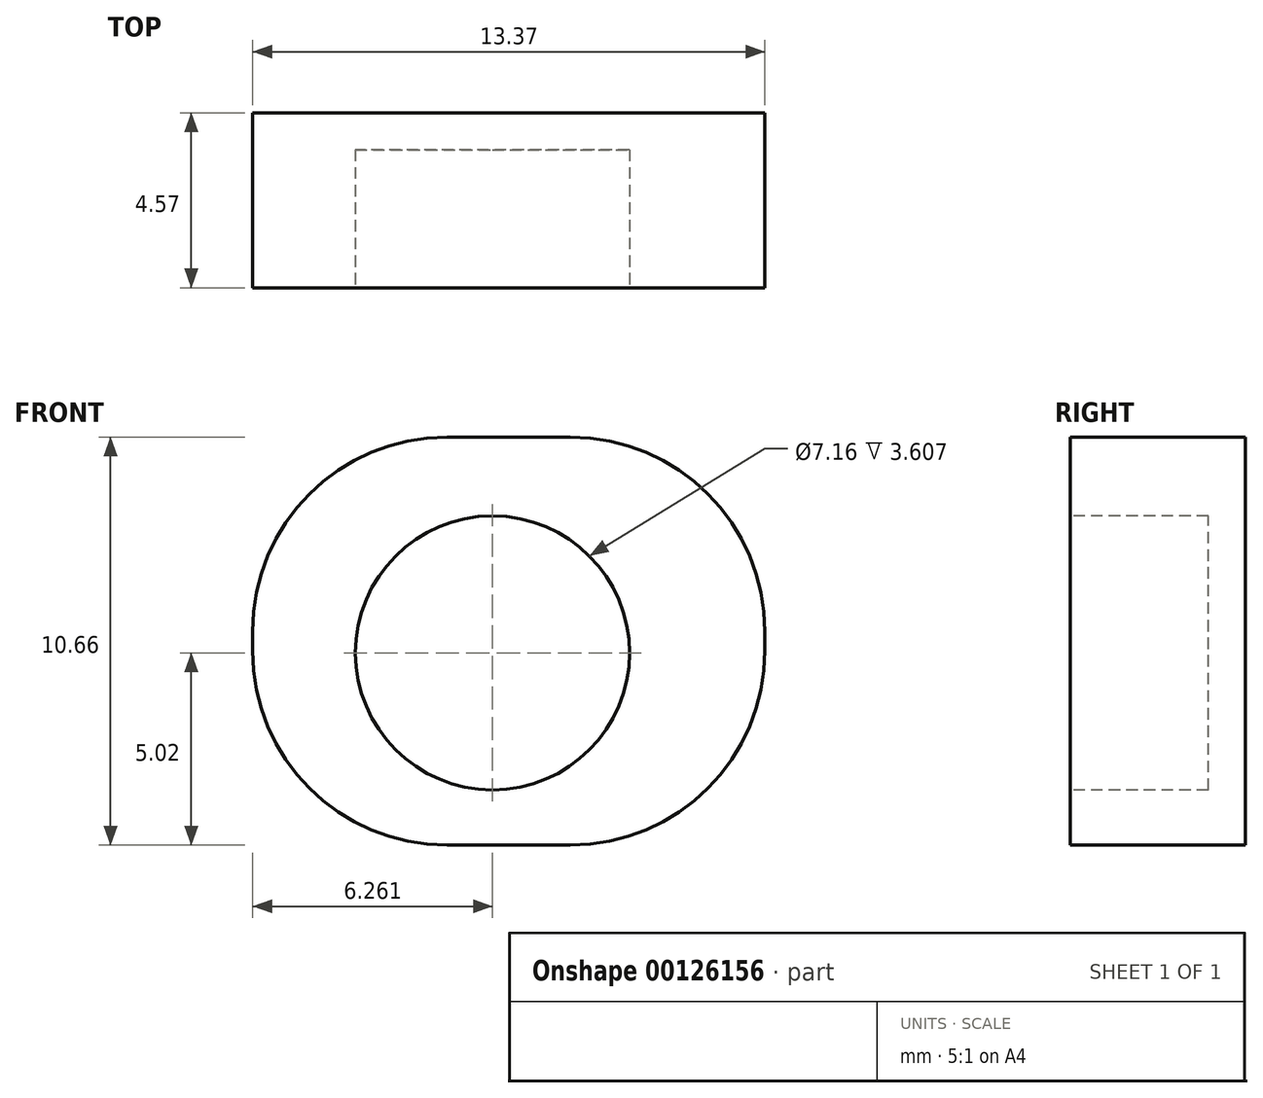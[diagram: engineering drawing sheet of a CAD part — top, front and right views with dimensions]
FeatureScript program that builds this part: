
annotation { "Feature Type Name" : "Feature", "Feature Type Description" : "" }
export const myFeature = defineFeature(function(context is Context, id is Id, definition is map)
    precondition{}
    {
        {
            var Q0;
            Q0=qCreatedBy(makeId("Front.planeOp"),FACE);
            var sketch = newSketch(context, id + "F0", { "sketchPlane" : qUnion([Q0])});
            skLineSegment(sketch, "E0.bottom", {"start": v(-10.53, -5.02) * mm, "end": v(2.84, -5.02) * mm});
            skLineSegment(sketch, "E0.top", {"start": v(-10.53, 5.64) * mm, "end": v(2.84, 5.64) * mm});
            skLineSegment(sketch, "E0.left", {"start": v(-10.53, -5.02) * mm, "end": v(-10.53, 5.64) * mm});
            skLineSegment(sketch, "E0.right", {"start": v(2.84, -5.02) * mm, "end": v(2.84, 5.64) * mm});
            skSolve(sketch);
        }
        {
            var Q0;
            Q0 = qSketchRegion(id + "F0", true);
            extrude(context, id + "F1", {"entities" : qUnion([Q0]), "depth" : 4.57 * mm});
        }
        {
            var Q0;
            Q0=makeQuery(id+"F1.opExtrude","CAP_FACE",FACE,{"disambiguationData":[OSD([sQuery(id+"F0.wireOp",EDGE,"E0.bottom"),sQuery(id+"F0.wireOp",EDGE,"E0.top"),sQuery(id+"F0.wireOp",EDGE,"E0.left"),sQuery(id+"F0.wireOp",EDGE,"E0.right")])],"isStart":false});
            var sketch = newSketch(context, id + "F2", { "sketchPlane" : qUnion([Q0])});
            skCircle(sketch, "E1", {"center": v(-4.27, 0) * mm, "radius": 3.58 * mm});
            skSolve(sketch);
        }
        {
            var Q0;
            Q0=makeQuery(id+"F2.imprint","IMPRINT",FACE,{"disambiguationData":[TD([[makeQuery(id+"F2.imprint","IMPRINT",EDGE,{"derivedFrom":sQuery(id+"F2.wireOp",EDGE,"E1")}),1.0]])]});
            extrude(context, id + "F3", {"entities" : qUnion([Q0]), "operationType" : NewBodyOperationType.REMOVE, "oppositeDirection" : true, "depth" : 3.6 * mm});
        }
        {
            var Q0;
            Q0=makeQuery(id+"F1.opExtrude","SWEPT_EDGE",EDGE,{"disambiguationData":[OSD([sQuery(id+"F0.wireOp",EDGE,"E0.bottom"),sQuery(id+"F0.wireOp",EDGE,"E0.right")])]});
            var Q1;
            Q1=makeQuery(id+"F1.opExtrude","SWEPT_EDGE",EDGE,{"disambiguationData":[OSD([sQuery(id+"F0.wireOp",EDGE,"E0.top"),sQuery(id+"F0.wireOp",EDGE,"E0.right")])]});
            var Q2;
            Q2=makeQuery(id+"F1.opExtrude","SWEPT_EDGE",EDGE,{"disambiguationData":[OSD([sQuery(id+"F0.wireOp",EDGE,"E0.top"),sQuery(id+"F0.wireOp",EDGE,"E0.left")])]});
            var Q3;
            Q3=makeQuery(id+"F1.opExtrude","SWEPT_EDGE",EDGE,{"disambiguationData":[OSD([sQuery(id+"F0.wireOp",EDGE,"E0.bottom"),sQuery(id+"F0.wireOp",EDGE,"E0.left")])]});
            fillet(context, id + "F4", {"entities" : qUnion([Q0, Q1, Q2, Q3]), "radius" : 5.08 * mm, "tangentPropagation" : true, "allowEdgeOverflow" : false});
        }
    });
